# Revit family: 1407xxx Micro Recess Switched
name_source: partatom
category: Lighting Fixtures
revit_build: Autodesk Revit 2018 (Build: 20170223_1515(x64)
units: mm (PartAtom-declared; Revit-internal decimal feet)

## family parameters
Always vertical = Yes
Cut with Voids When Loaded = No
Host = Wall
Light Source = Yes
OmniClass Number = 23.80.70.00
OmniClass Title = Lighting
Part Type = Normal
Room Calculation Point = No
Round Connector Dimension = Use Diameter
Shared = No

## types (2) — shared parameters
Color Filter = 16777215
Dimmable = No
Dimming Lamp Color Temperature Shift = <None>
Driver Included = Yes
Driver Required = No
Lamp = LED
Light Source Fixed = Yes
Manufacturer = Astro Lighting Ltd
Photometric Web File = IES_L17947 Micro Recess Switched Luminaire.ies
Product Location = Indoor
Product Name = Micro Recess Switched
Tilt Angle = 90.00°
URL = www.astrolighting.com

## per-type parameters (varying)
| type | ADA compliant | Apparent Load | Dimming Method | Efficacy (lm/w) | Electrical Class | Location rating | Main Finish | Main Material | Power (Watts) | Product Code | Product SKU | Wattage Comments |
| CE |  | 6 VA |  | 49 | CE (Class I) | IP20 | Various | Metal - Steel | 3.4 |  | 1407006 |  |
| ETL | Yes | 5 VA | Not Applicable | 61 | cETLus (Class 1) | DAMP | Matt White | Metal - Mild Steel | 3.2 | 8639 | 1407016 | Measured |

## geometry (parser evidence)
native form markers: Sweep x1
no freeform markers — native parametric forms only
